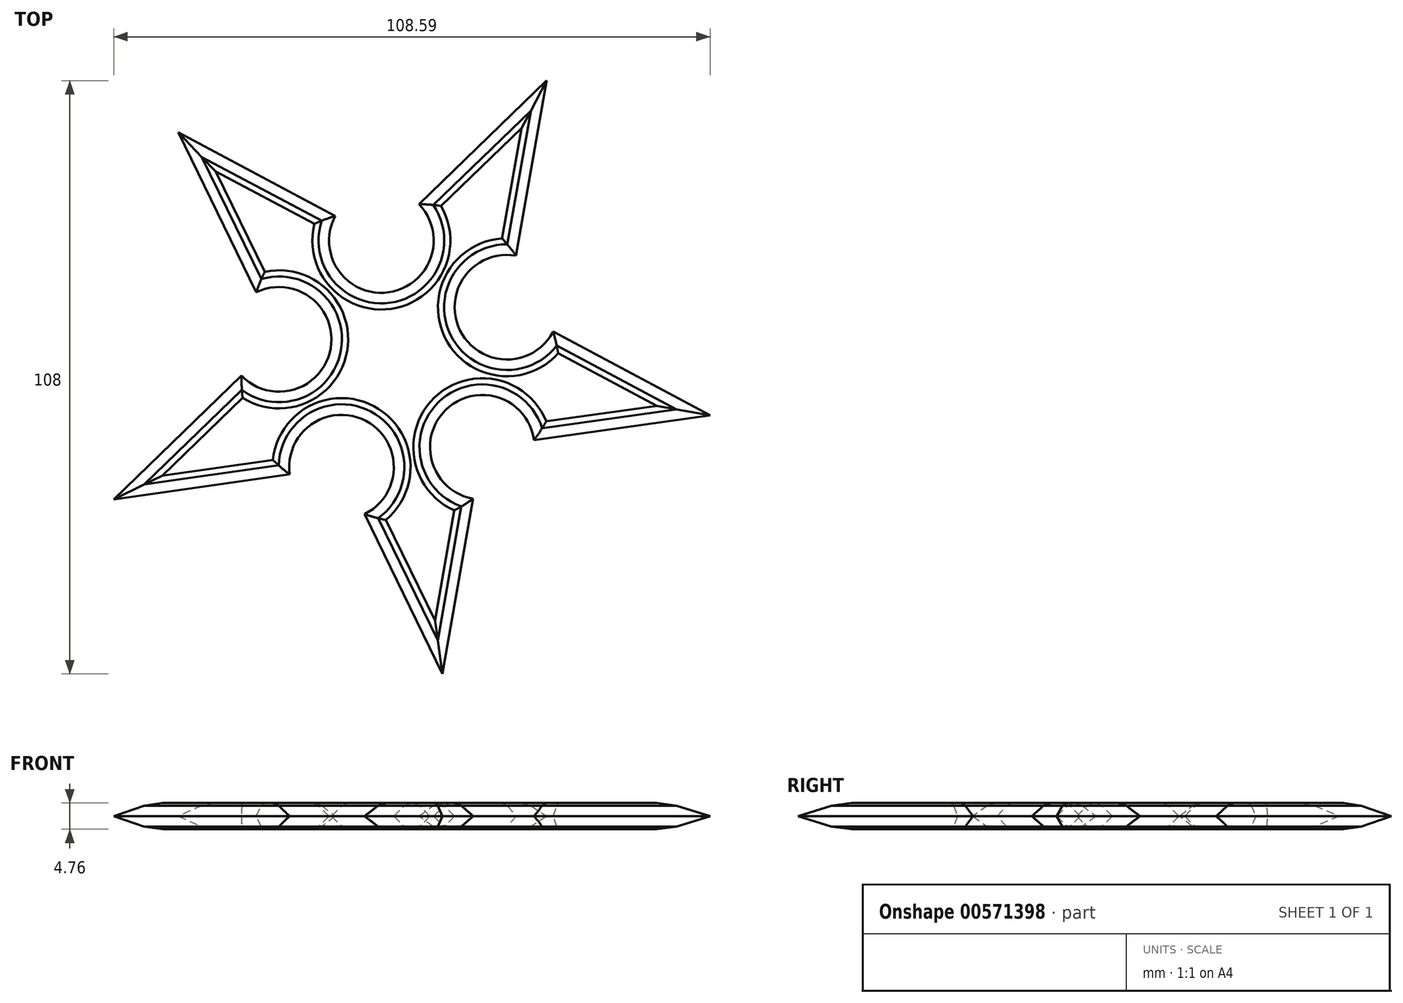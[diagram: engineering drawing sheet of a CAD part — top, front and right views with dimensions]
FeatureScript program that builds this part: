
annotation { "Feature Type Name" : "Feature", "Feature Type Description" : "" }
export const myFeature = defineFeature(function(context is Context, id is Id, definition is map)
    precondition{}
    {
        {
            var Q0;
            Q0=qCreatedBy(makeId("Top.planeOp"),FACE);
            var sketch = newSketch(context, id + "F0", { "sketchPlane" : qUnion([Q0])});
            skCircle(sketch, "E0.cCircle", {"center": v(0, 0) * mm, "radius": 46.64 * mm, "construction": true});
            skLineSegment(sketch, "E0.0", {"start": v(27.04, 50.91) * mm, "end": v(56.78, -9.99) * mm, "construction": true});
            skLineSegment(sketch, "E0.1", {"start": v(56.78, -9.99) * mm, "end": v(8.05, -57.09) * mm, "construction": true});
            skLineSegment(sketch, "E0.2", {"start": v(8.05, -57.09) * mm, "end": v(-51.8, -25.3) * mm, "construction": true});
            skLineSegment(sketch, "E0.3", {"start": v(-51.8, -25.3) * mm, "end": v(-40.07, 41.45) * mm, "construction": true});
            skLineSegment(sketch, "E0.4", {"start": v(-40.07, 41.45) * mm, "end": v(27.04, 50.91) * mm, "construction": true});
            skPoint(sketch, "E0.0.midPoint", {"position": v(41.91, 20.46) * mm});
            skLineSegment(sketch, "E1", {"start": v(-40.07, 41.45) * mm, "end": v(-21.69, 3.81) * mm});
            skLineSegment(sketch, "E2", {"start": v(27.04, 50.91) * mm, "end": v(19.79, 9.66) * mm});
            skLineSegment(sketch, "E3", {"start": v(-51.8, -25.3) * mm, "end": v(-10.33, -19.45) * mm});
            skLineSegment(sketch, "E4", {"start": v(-40.07, 41.45) * mm, "end": v(-3.07, 21.8) * mm});
            skLineSegment(sketch, "E5", {"start": v(-51.8, -25.3) * mm, "end": v(-21.69, 3.81) * mm});
            skLineSegment(sketch, "E6.trimOffspring", {"start": v(-3.07, 21.8) * mm, "end": v(27.04, 50.91) * mm});
            skLineSegment(sketch, "E7.trimOffspring", {"start": v(-10.33, -19.45) * mm, "end": v(8.05, -57.09) * mm});
            skLineSegment(sketch, "E8.trimOffspring", {"start": v(19.79, 9.66) * mm, "end": v(56.78, -9.99) * mm});
            skLineSegment(sketch, "E9.trimOffspring", {"start": v(15.3, -15.83) * mm, "end": v(8.05, -57.09) * mm});
            skLineSegment(sketch, "E10.trimOffspring", {"start": v(15.3, -15.83) * mm, "end": v(56.78, -9.99) * mm});
            skSolve(sketch);
        }
        {
            var Q0;
            Q0=qSketchRegion(id+"F0",true);
            extrude(context, id + "F1", {"entities" : qUnion([Q0]), "depth" : 4.76 * mm});
        }
        {
            var Q0;
            Q0=qCreatedBy(makeId("Top.planeOp"),FACE);
            var sketch = newSketch(context, id + "F2", { "sketchPlane" : qUnion([Q0])});
            skCircle(sketch, "E11", {"center": v(15.3, -15.83) * mm, "radius": 9.53 * mm});
            skCircle(sketch, "E12", {"center": v(-10.33, -19.45) * mm, "radius": 9.53 * mm});
            skCircle(sketch, "E13", {"center": v(-21.69, 3.81) * mm, "radius": 9.53 * mm});
            skCircle(sketch, "E14", {"center": v(-3.07, 21.8) * mm, "radius": 9.53 * mm});
            skCircle(sketch, "E15", {"center": v(19.79, 9.66) * mm, "radius": 9.53 * mm});
            skSolve(sketch);
        }
        {
            var Q0;
            Q0=qSketchRegion(id+"F2",true);
            extrude(context, id + "F3", {"entities" : qUnion([Q0]), "operationType" : NewBodyOperationType.REMOVE, "endBound" : BoundingType.THROUGH_ALL, "depth" : 25.4 * mm});
        }
        {
            var Q0;
            Q0=makeQuery(id+"F1.opExtrude","CAP_FACE",FACE,{"disambiguationData":[OSD([sQuery(id+"F0.wireOp",EDGE,"E1"),sQuery(id+"F0.wireOp",EDGE,"E2"),sQuery(id+"F0.wireOp",EDGE,"E3"),sQuery(id+"F0.wireOp",EDGE,"E4"),sQuery(id+"F0.wireOp",EDGE,"E5"),sQuery(id+"F0.wireOp",EDGE,"E6.trimOffspring"),sQuery(id+"F0.wireOp",EDGE,"E7.trimOffspring"),sQuery(id+"F0.wireOp",EDGE,"E8.trimOffspring"),sQuery(id+"F0.wireOp",EDGE,"E9.trimOffspring"),sQuery(id+"F0.wireOp",EDGE,"E10.trimOffspring")])],"isStart":false});
            var Q1;
            Q1=makeQuery(id+"F1.opExtrude","CAP_FACE",FACE,{"disambiguationData":[OSD([sQuery(id+"F0.wireOp",EDGE,"E1"),sQuery(id+"F0.wireOp",EDGE,"E2"),sQuery(id+"F0.wireOp",EDGE,"E3"),sQuery(id+"F0.wireOp",EDGE,"E4"),sQuery(id+"F0.wireOp",EDGE,"E5"),sQuery(id+"F0.wireOp",EDGE,"E6.trimOffspring"),sQuery(id+"F0.wireOp",EDGE,"E7.trimOffspring"),sQuery(id+"F0.wireOp",EDGE,"E8.trimOffspring"),sQuery(id+"F0.wireOp",EDGE,"E9.trimOffspring"),sQuery(id+"F0.wireOp",EDGE,"E10.trimOffspring")])],"isStart":true});
            chamfer(context, id + "F4", {"entities" : qUnion([Q0, Q1]), "width" : 2.38 * mm, "tangentPropagation" : true});
        }
        {
            var Q0;
            Q0=makeQuery(id+"F1.opExtrude","CAP_FACE",FACE,{"disambiguationData":[OSD([sQuery(id+"F0.wireOp",EDGE,"E1"),sQuery(id+"F0.wireOp",EDGE,"E2"),sQuery(id+"F0.wireOp",EDGE,"E3"),sQuery(id+"F0.wireOp",EDGE,"E4"),sQuery(id+"F0.wireOp",EDGE,"E5"),sQuery(id+"F0.wireOp",EDGE,"E6.trimOffspring"),sQuery(id+"F0.wireOp",EDGE,"E7.trimOffspring"),sQuery(id+"F0.wireOp",EDGE,"E8.trimOffspring"),sQuery(id+"F0.wireOp",EDGE,"E9.trimOffspring"),sQuery(id+"F0.wireOp",EDGE,"E10.trimOffspring")])],"isStart":false});
            var Q1;
            Q1=makeQuery(id+"F1.opExtrude","CAP_FACE",FACE,{"disambiguationData":[OSD([sQuery(id+"F0.wireOp",EDGE,"E1"),sQuery(id+"F0.wireOp",EDGE,"E2"),sQuery(id+"F0.wireOp",EDGE,"E3"),sQuery(id+"F0.wireOp",EDGE,"E4"),sQuery(id+"F0.wireOp",EDGE,"E5"),sQuery(id+"F0.wireOp",EDGE,"E6.trimOffspring"),sQuery(id+"F0.wireOp",EDGE,"E7.trimOffspring"),sQuery(id+"F0.wireOp",EDGE,"E8.trimOffspring"),sQuery(id+"F0.wireOp",EDGE,"E9.trimOffspring"),sQuery(id+"F0.wireOp",EDGE,"E10.trimOffspring")])],"isStart":true});
            chamfer(context, id + "F5", {"entities" : qUnion([Q0, Q1]), "width" : 1.59 * mm, "tangentPropagation" : true});
        }
    });
